# Revit family: Legrand Armoire XL³ 6300-4000
name_source: partatom
category: Equipement électrique
units: mm (PartAtom-declared; Revit-internal decimal feet)

## family parameters
Basée sur le plan de construction = Non
Configuration du panneau = Deux colonnes, circuits au sein
Cote de connecteur circulaire = Utiliser le diamètre
Couper avec des vides une fois chargée = Non
Numéro OmniClass = 23.80.30.11.17
Partagée = Non
Point de calcul de pièce = Non
Titre OmniClass = Distribution Boards and Control Panels
Toujours verticalement = Oui
Type d'élément = Tableau de raccordement

## types (15) — shared parameters
Conditions Générale d'Utilisation = https://export.legrand.com
Fabricant = Legrand
Finition = revétu de poudre
Forme de séparation jusqu'à (jusqu'à) = 4b
ICW (jusqu'à) = 110
IK sans porte = 07
IP sans porte = 30
Matière = Acier
Modèle = XL³ 4000
RAL = 7035
zero-valued in all types: Elévation par défaut

## per-type parameters (varying)
| type | Hauteur (mm) | IK avec porte | IN max (A) | IP avec porte | Largeur (mm) | URL | porte | profondeur (mm) |
| 020504-020500-020514-020554 | 2000 mm  [stored 6.56168 ft] | 08 | 4000 | 55 | 725 mm  [stored 2.37861 ft] | https://www.legrand.fr | Oui | 475 mm  [stored 1.5584 ft] |
| 020504-020850-020514-020861 | 2200 mm | 08 | 4000 | 55 | 725 mm  [stored 2.37861 ft] | https://www.legrand.fr | Oui | 475 mm  [stored 1.5584 ft] |
| 020505-020500-020515-020554 | 2000 mm  [stored 6.56168 ft] | 08 | 4000 | 55 | 725 mm  [stored 2.37861 ft] | https://www.legrand.fr | Oui | 725 mm  [stored 2.37861 ft] |
| 020505-020850-020515-020861 | 2200 mm | 08 | 4000 | 55 | 725 mm  [stored 2.37861 ft] | https://www.legrand.fr | Oui | 725 mm  [stored 2.37861 ft] |
| 020506-020500-020516-020554 | 2000 mm  [stored 6.56168 ft] | 08 | 4000 | 55 | 725 mm  [stored 2.37861 ft] | https://www.legrand.fr | Oui | 975 mm  [stored 3.19882 ft] |
| 020506-020850-020516-020861 | 2200 mm | 08 | 4000 | 55 | 725 mm  [stored 2.37861 ft] | https://www.legrand.fr | Oui | 975 mm  [stored 3.19882 ft] |
| 020507-020500-020517-020554 | 2000 mm  [stored 6.56168 ft] | 08 | 4000 | 55 | 975 mm  [stored 3.19882 ft] | https://www.legrand.fr | Oui | 475 mm  [stored 1.5584 ft] |
| 020507-020850-020517-020861 | 2200 mm | 08 | 4000 | 55 | 975 mm  [stored 3.19882 ft] | https://www.legrand.fr
https://www.legrand.fr | Oui | 475 mm  [stored 1.5584 ft] |
| 020508-020500-020518-020554 | 2000 mm  [stored 6.56168 ft] | 08 | 4000 | 55 | 975 mm  [stored 3.19882 ft] | https://www.legrand.fr | Oui | 725 mm  [stored 2.37861 ft] |
| 020508-020850-020518-020861 | 2200 mm | 08 | 4000 | 55 | 975 mm  [stored 3.19882 ft] | https://www.legrand.fr | Oui | 725 mm  [stored 2.37861 ft] |
| 020509-020500-020519-020554 | 2000 mm  [stored 6.56168 ft] | 08 | 4000 | 55 | 975 mm  [stored 3.19882 ft] | https://www.legrand.fr | Oui | 975 mm  [stored 3.19882 ft] |
| 020509-020850-020519-020861 | 2200 mm | 08 | 4000 | 55 | 975 mm  [stored 3.19882 ft] | https://www.legrand.fr | Oui | 975 mm  [stored 3.19882 ft] |
| 021133-021136-021130 | 2200 mm |  | 6300 |  | 1425 mm  [stored 4.6752 ft] | https://www.legrand.fr | Non | 475 mm  [stored 1.5584 ft] |
| 021134-021136-021131 | 2200 mm |  | 6300 |  | 1425 mm  [stored 4.6752 ft] | https://www.legrand.fr | Non | 725 mm  [stored 2.37861 ft] |
| 021135-021136-021132 | 2200 mm |  | 6300 |  | 1425 mm  [stored 4.6752 ft] | https://www.legrand.fr | Non | 975 mm  [stored 3.19882 ft] |

note: [stored X ft] marks values corroborated as IEEE doubles in the binary element streams (Revit-internal decimal feet)
